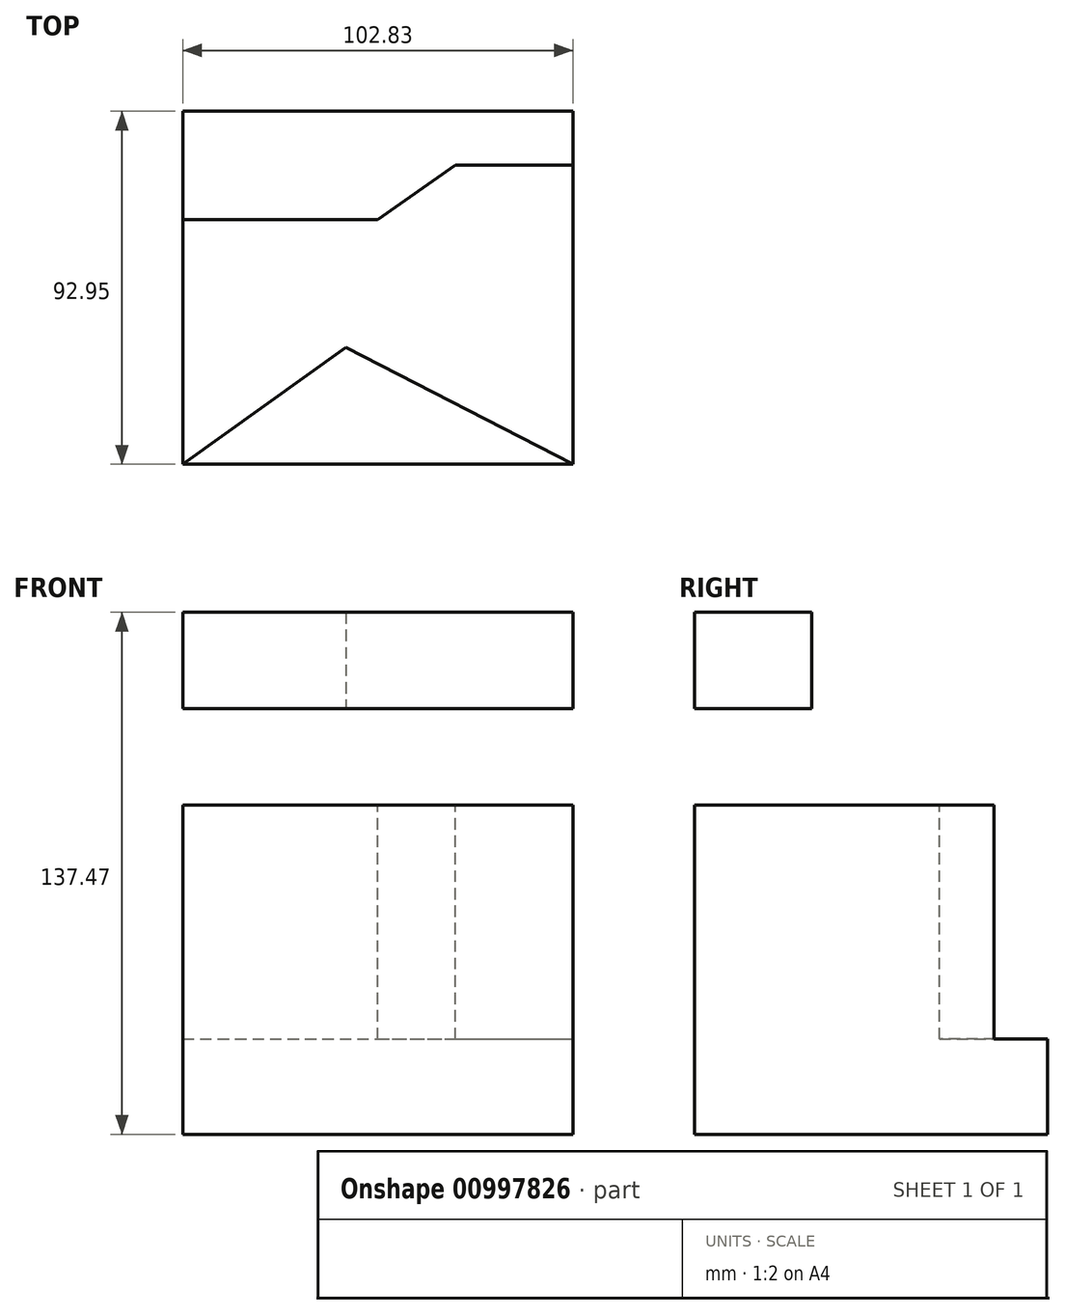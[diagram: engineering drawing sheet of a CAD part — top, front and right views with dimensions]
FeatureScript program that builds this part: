
annotation { "Feature Type Name" : "Feature", "Feature Type Description" : "" }
export const myFeature = defineFeature(function(context is Context, id is Id, definition is map)
    precondition{}
    {
        {
            var Q0;
            Q0=qCreatedBy(makeId("Top.planeOp"),FACE);
            var sketch = newSketch(context, id + "F0", { "sketchPlane" : qUnion([Q0])});
            skLineSegment(sketch, "E0.bottom", {"start": v(-43, 40.77) * mm, "end": v(59.83, 40.77) * mm});
            skLineSegment(sketch, "E0.top", {"start": v(-43, -52.18) * mm, "end": v(59.83, -52.18) * mm});
            skLineSegment(sketch, "E0.left", {"start": v(-43, 40.77) * mm, "end": v(-43, -52.18) * mm});
            skLineSegment(sketch, "E0.right", {"start": v(59.83, 40.77) * mm, "end": v(59.83, -52.18) * mm});
            skSolve(sketch);
        }
        {
            var Q0;
            Q0=makeQuery(id+"F0.imprint","IMPRINT",FACE,{"disambiguationData":[TD([[makeQuery(id+"F0.imprint","IMPRINT",EDGE,{"derivedFrom":sQuery(id+"F0.wireOp",EDGE,"E0.bottom")}),-1.0]])]});
            extrude(context, id + "F1", {"entities" : qUnion([Q0]), "depth" : 86.67 * mm, "offsetDistance" : 25.4 * mm});
        }
        {
            var Q0;
            Q0=makeQuery(id+"F1.opExtrude","CAP_FACE",FACE,{"disambiguationData":[OSD([sQuery(id+"F0.wireOp",EDGE,"E0.bottom"),sQuery(id+"F0.wireOp",EDGE,"E0.top"),sQuery(id+"F0.wireOp",EDGE,"E0.left"),sQuery(id+"F0.wireOp",EDGE,"E0.right")])],"isStart":false});
            var sketch = newSketch(context, id + "F2", { "sketchPlane" : qUnion([Q0])});
            skLineSegment(sketch, "E1", {"start": v(-43, 12.24) * mm, "end": v(8.41, 12.24) * mm});
            skPoint(sketch, "E1.endSnap0", {"position": v(8.41, 40.77) * mm});
            skLineSegment(sketch, "E2", {"start": v(8.41, 12.24) * mm, "end": v(28.83, 26.6) * mm});
            skLineSegment(sketch, "E3", {"start": v(28.83, 26.6) * mm, "end": v(59.83, 26.6) * mm});
            skSolve(sketch);
        }
        {
            var Q0;
            {var subQ2=sQuery(id+"F2.wireOp",EDGE,"E1");Q0=makeQuery(id+"F2.imprint","IMPRINT",FACE,{"disambiguationData":[TD([[makeQuery(id+"F2.imprint","IMPRINT",EDGE,{"derivedFrom":subQ2}),1.0]])]});}
            extrude(context, id + "F3", {"entities" : qUnion([Q0]), "operationType" : NewBodyOperationType.REMOVE, "oppositeDirection" : true, "depth" : 61.6 * mm, "offsetDistance" : 25.4 * mm});
        }
        {
            var Q0;
            Q0=makeQuery(id+"F1.opExtrude","CAP_FACE",FACE,{"disambiguationData":[OSD([sQuery(id+"F0.wireOp",EDGE,"E0.bottom"),sQuery(id+"F0.wireOp",EDGE,"E0.top"),sQuery(id+"F0.wireOp",EDGE,"E0.left"),sQuery(id+"F0.wireOp",EDGE,"E0.right")])],"isStart":false});
            cPlane(context, id + "F4", {"entities" : qUnion([Q0]), "cplaneType" : CPlaneType.OFFSET, "offset" : 25.4 * mm, "width" : 152.4 * mm, "height" : 152.4 * mm});
        }
        {
            var Q0;
            Q0=qCreatedBy(id+"F4.planeOp",FACE);
            var sketch = newSketch(context, id + "F5", { "sketchPlane" : qUnion([Q0])});
            skLineSegment(sketch, "E4.0.0", {"start": v(59.83, 26.6) * mm, "end": v(28.83, 26.6) * mm});
            skLineSegment(sketch, "E4.0.1", {"start": v(28.83, 26.6) * mm, "end": v(8.41, 12.24) * mm});
            skLineSegment(sketch, "E4.0.2", {"start": v(8.41, 12.24) * mm, "end": v(-43, 12.24) * mm});
            skLineSegment(sketch, "E4.0.3", {"start": v(-43, 12.24) * mm, "end": v(-43, -52.18) * mm});
            skLineSegment(sketch, "E4.0.4", {"start": v(-43, -52.18) * mm, "end": v(59.83, -52.18) * mm});
            skLineSegment(sketch, "E4.0.5", {"start": v(59.83, -52.18) * mm, "end": v(59.83, 26.6) * mm});
            skLineSegment(sketch, "E5", {"start": v(-43, -52.18) * mm, "end": v(0, -21.38) * mm});
            skLineSegment(sketch, "E6", {"start": v(0, -21.38) * mm, "end": v(59.83, -52.18) * mm});
            skSolve(sketch);
        }
        {
            var Q0;
            Q0=makeQuery(id+"F5.imprint","IMPRINT",FACE,{"disambiguationData":[TD([[makeQuery(id+"F5.imprint","IMPRINT",EDGE,{"derivedFrom":sQuery(id+"F5.wireOp",EDGE,"E4.0.4")}),1.0]])]});
            extrude(context, id + "F6", {"entities" : qUnion([Q0]), "depth" : 25.4 * mm, "offsetDistance" : 25.4 * mm});
        }
    });
